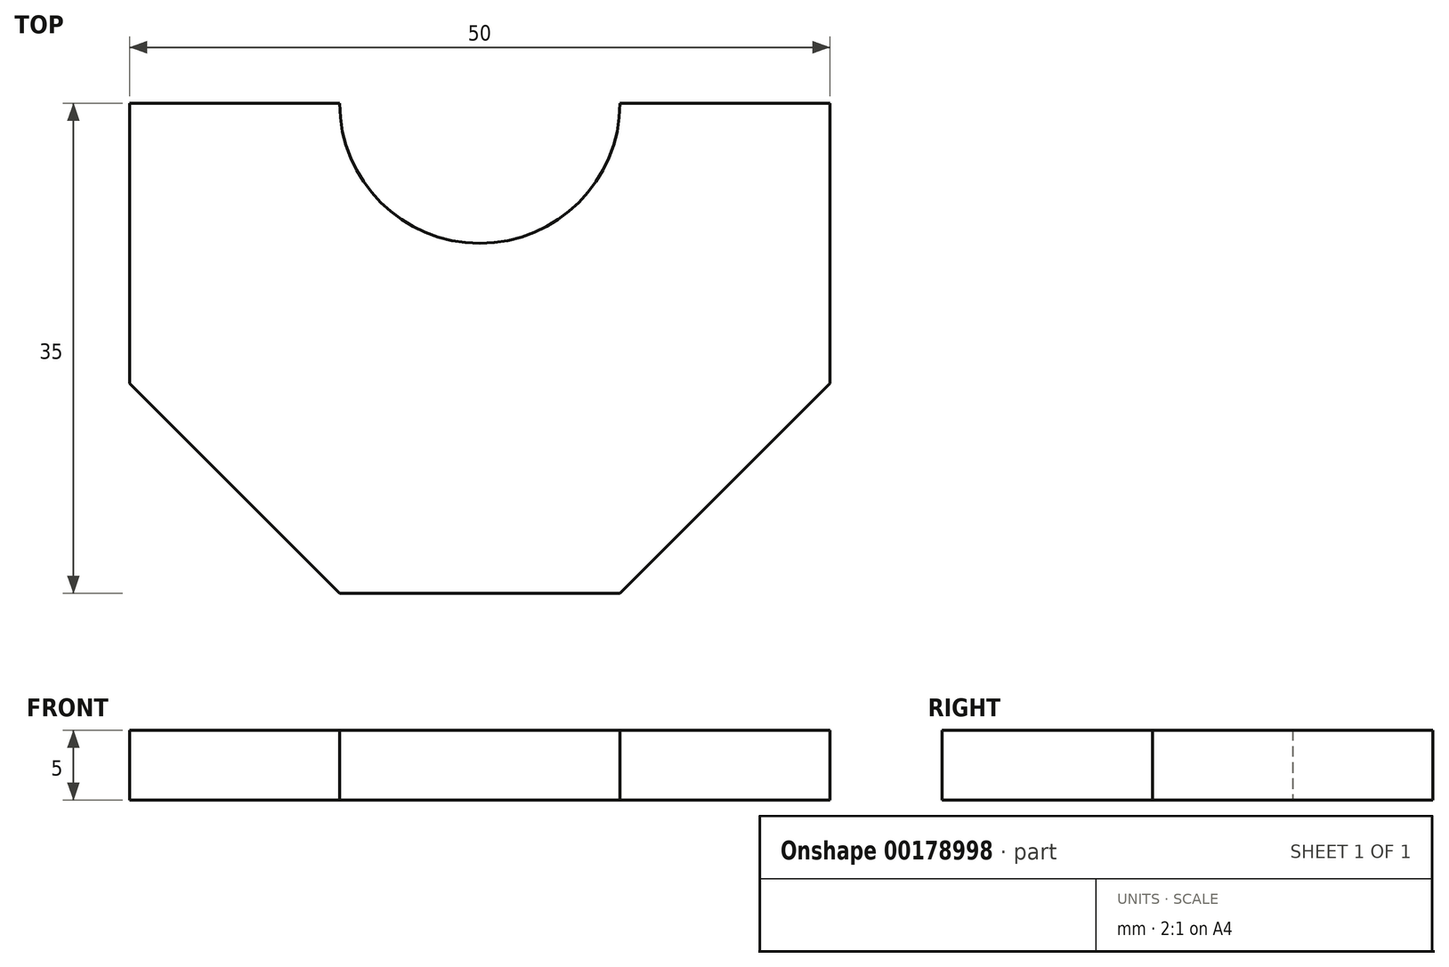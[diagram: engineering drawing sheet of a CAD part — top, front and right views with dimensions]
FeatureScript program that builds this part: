
annotation { "Feature Type Name" : "Feature", "Feature Type Description" : "" }
export const myFeature = defineFeature(function(context is Context, id is Id, definition is map)
    precondition{}
    {
        {
            var Q0;
            Q0=qCreatedBy(makeId("Top.planeOp"),FACE);
            var sketch = newSketch(context, id + "F0", { "sketchPlane" : qUnion([Q0])});
            skLineSegment(sketch, "E0.bottom", {"start": v(25, -17.5) * mm, "end": v(-25, -17.5) * mm});
            skLineSegment(sketch, "E0.top", {"start": v(25, 17.5) * mm, "end": v(-25, 17.5) * mm});
            skLineSegment(sketch, "E0.left", {"start": v(25, -17.5) * mm, "end": v(25, 17.5) * mm});
            skLineSegment(sketch, "E0.right", {"start": v(-25, -17.5) * mm, "end": v(-25, 17.5) * mm});
            skPoint(sketch, "E0.middle", {"position": v(0, 0) * mm});
            skLineSegment(sketch, "E1", {"start": v(25, -2.5) * mm, "end": v(10, -17.5) * mm});
            skLineSegment(sketch, "E2", {"start": v(-25, -2.5) * mm, "end": v(-10, -17.5) * mm});
            skCircle(sketch, "E3", {"center": v(0, 17.5) * mm, "radius": 10 * mm});
            skSolve(sketch);
        }
        {
            var Q0;
            {var subQ3=sQuery(id+"F0.wireOp",EDGE,"E1");Q0=makeQuery(id+"F0.imprint","IMPRINT",FACE,{"disambiguationData":[TD([[makeQuery(id+"F0.imprint","IMPRINT",EDGE,{"derivedFrom":subQ3}),-1.0]])]});}
            extrude(context, id + "F1", {"entities" : qUnion([Q0]), "depth" : 5 * mm});
        }
    });
